# Revit family: 0047432 Feilo Sylvania Lighting Fixture START FLAT PANEL LED 1200x600 NW
name_source: partatom
category: Lighting Fixtures
revit_build: Autodesk Revit 2017 (Build: 20190507_1515(x64)
units: mm (PartAtom-declared; Revit-internal decimal feet)

## family parameters
Cut with Voids When Loaded = No
Host = Face
Light Source = No
OmniClass Number = 23.80.70.00
OmniClass Title = Lighting
Part Type = Normal
Room Calculation Point = No
Round Connector Dimension = Use Diameter
Shared = No

## types (1)
- 0047432_5300LM_60W
    AccessoryMaterial = <By Category>
    Apparent Load = 60 VA
    Assembly Code = D5020200
    BeamAngle = 120.00°
    BodyMaterial = Body-Sylvania_White
    ClassificationName = Uniclass2015
    ClassificationValue = EF_70_80
    Color = White
    ColorConsistency(SDCM) = 3
    ControlGearType = Electrical
    Cost = 0 $
    Default Elevation = 1219 mm
    Diffuser Finish = Opal
    Diffuser Material = Acrylic PMMA
    DiffuserMaterial = Diffuser-Sylvania-Glow
    DimmingControlOptions = Non dimmable
    DistributionType = Direct
    DocumentationLiterature = http://www.sylvania-lighting.com
    DriveCurrent = 2 A
    DurationUnit = hrs
    ElectricShockClassification = Class II
    ExpectedLife = 50000
    GlareControl = UGR<25
    IfcExportAs = IfcLightFixtureType
    IfcExportType = IfcLightFixtureType
    ImpactProtectionIndex = IK05
    IngressProtection = IP20
    InputNominalFrequency = 50/60 Hz
    InputVoltage = 220-240V
    InrushCurrent = 14 A
    InrushDuration = 0.16 ms
    Keynote = EF_70_80
    LampColourTemperature = 4000 K
    LampsType = LED
    LightColour = Neutral white
    LightOutputRatio = 100
    LuminaireEfficacy = 88 lm/W
    LuminousFlux = 5300 lm
    Manufacturer = Feilo Sylvania
    ManufacturerName = Feilo Sylvania
    Model = START FLAT PANEL LED 1200X600 NW
    ModelNumber = 0047432
    ModelReference = Start Flat Panel LED
    NominalDepth = 595 mm
    NominalHeight = 11 mm
    NominalLength = 1196 mm  [stored 3.92388 ft]
    PhotobiologicalRiskGroup = RG0
    PowerConsumption = 60 W
    PowerFactor = 0
    ReflectorMaterial = <By Category>
    Type Image = <None>
    TypeName = Start Flat Panel LED 1200X600
    URL = http://www.sylvania-lighting.com
    Voltage = 230 V
    WarrantyDurationUnit = year
    Weight = 6.044 kg
    _BimSpecGuid = 0
    _BimstoreBibleVersion = Version 15
    _CurrentRevision = 0

note: [stored X ft] marks values corroborated as IEEE doubles in the binary element streams (Revit-internal decimal feet)

## geometry (parser evidence)
native form markers: Sweep x4
no freeform markers — native parametric forms only
